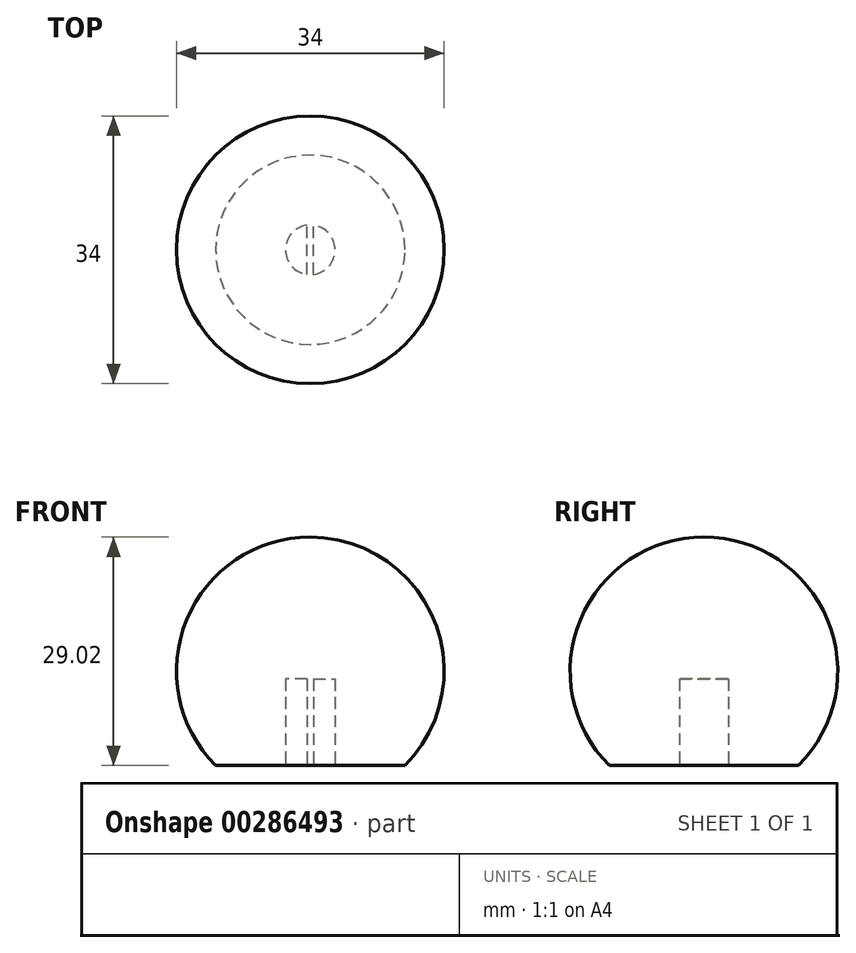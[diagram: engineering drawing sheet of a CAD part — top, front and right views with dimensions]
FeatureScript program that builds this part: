
annotation { "Feature Type Name" : "Feature", "Feature Type Description" : "" }
export const myFeature = defineFeature(function(context is Context, id is Id, definition is map)
    precondition{}
    {
        {
            var Q0;
            Q0=qCreatedBy(makeId("Front.planeOp"),FACE);
            var sketch = newSketch(context, id + "F0", { "sketchPlane" : qUnion([Q0])});
            skArc(sketch, "E0", {"start": v(0, 17) * mm, "mid": v(17, 0) * mm, "end": v(0, -17) * mm});
            skLineSegment(sketch, "E1", {"start": v(0, 17) * mm, "end": v(0, -17) * mm});
            skLineSegment(sketch, "E2", {"start": v(0, -12.02) * mm, "end": v(12.02, -12.02) * mm});
            skLineSegment(sketch, "E3", {"start": v(12.02, -12.02) * mm, "end": v(0, -24.04) * mm, "construction": true});
            skSolve(sketch);
        }
        {
            var Q0;
            {var subQ3=sQuery(id+"F0.wireOp",EDGE,"E2");Q0=makeQuery(id+"F0.imprint","IMPRINT",FACE,{"disambiguationData":[TD([[makeQuery(id+"F0.imprint","IMPRINT",EDGE,{"derivedFrom":subQ3}),1.0]])]});}
            var Q1;
            Q1=sQuery(id+"F0.wireOp",EDGE,"E1");
            revolve(context, id + "F1", {"surfaceOperationType" : NewSurfaceOperationType.NEW, "entities" : qUnion([Q0]), "axis" : qUnion([Q1]), "revolveType" : RevolveType.FULL});
        }
        {
            var Q0;
            Q0=makeQuery(id+"F1.opRevolve","SWEPT_FACE",FACE,{"disambiguationData":[OSD([sQuery(id+"F0.wireOp",EDGE,"E2")])]});
            var sketch = newSketch(context, id + "F2", { "sketchPlane" : qUnion([Q0])});
            skCircle(sketch, "E4", {"center": v(0, 0) * mm, "radius": 3.15 * mm});
            skLineSegment(sketch, "E5", {"start": v(-0.43, 3.12) * mm, "end": v(-0.42, -3.12) * mm});
            skLineSegment(sketch, "E6.MirrorCS", {"start": v(0.43, 3.12) * mm, "end": v(0.42, -3.12) * mm});
            skSolve(sketch);
        }
        {
            var Q0;
            {var subQ0=sQuery(id+"F2.wireOp",EDGE,"E5");Q0=makeQuery(id+"F2.imprint","IMPRINT",FACE,{"disambiguationData":[TD([[makeQuery(id+"F2.imprint","IMPRINT",EDGE,{"derivedFrom":subQ0}),-1.0]])]});}
            var Q1;
            {var subQ0=sQuery(id+"F2.wireOp",EDGE,"E6.MirrorCS");Q1=makeQuery(id+"F2.imprint","IMPRINT",FACE,{"disambiguationData":[TD([[makeQuery(id+"F2.imprint","IMPRINT",EDGE,{"derivedFrom":subQ0}),1.0]])]});}
            extrude(context, id + "F3", {"entities" : qUnion([Q0, Q1]), "operationType" : NewBodyOperationType.REMOVE, "oppositeDirection" : true, "depth" : 11 * mm, "offsetDistance" : 25 * mm});
        }
    });
